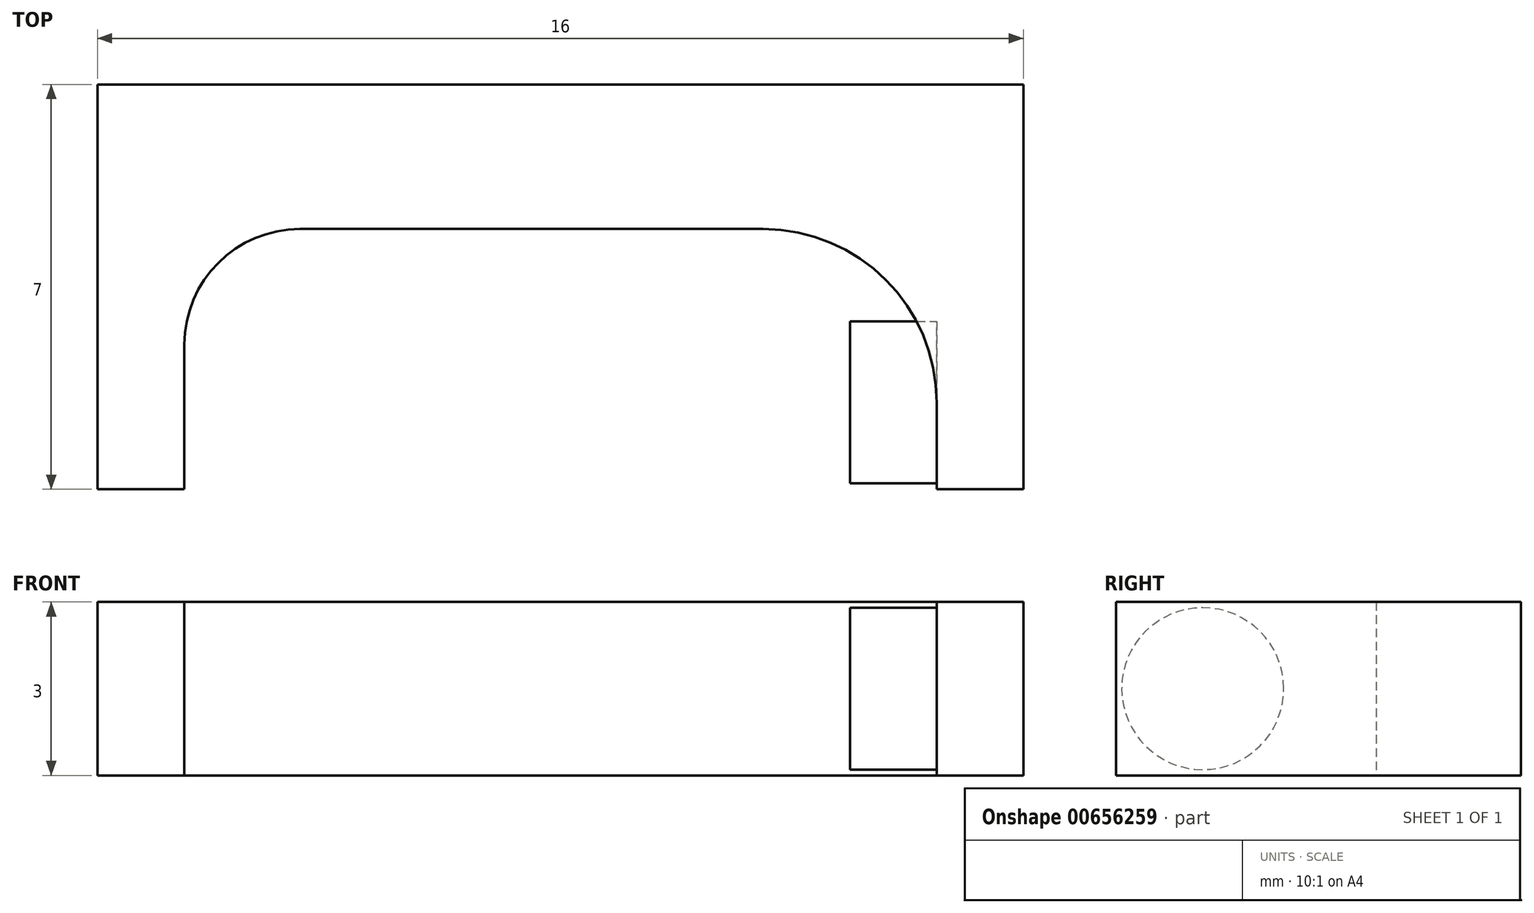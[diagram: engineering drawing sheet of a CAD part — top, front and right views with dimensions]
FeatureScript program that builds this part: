
annotation { "Feature Type Name" : "Feature", "Feature Type Description" : "" }
export const myFeature = defineFeature(function(context is Context, id is Id, definition is map)
    precondition{}
    {
        {
            var Q0;
            Q0=qCreatedBy(makeId("Top.planeOp"),FACE);
            var sketch = newSketch(context, id + "F0", { "sketchPlane" : qUnion([Q0])});
            skLineSegment(sketch, "E0", {"start": v(-1.74, -1) * mm, "end": v(-1.74, 3.5) * mm});
            skLineSegment(sketch, "E1", {"start": v(-1.74, 3.5) * mm, "end": v(11.26, 3.5) * mm});
            skLineSegment(sketch, "E2", {"start": v(11.26, 3.5) * mm, "end": v(11.26, -1) * mm});
            skLineSegment(sketch, "E3", {"start": v(-1.74, -1) * mm, "end": v(-3.24, -1) * mm});
            skLineSegment(sketch, "E4", {"start": v(-3.24, -1) * mm, "end": v(-3.24, 6) * mm});
            skLineSegment(sketch, "E5", {"start": v(-3.24, 6) * mm, "end": v(12.76, 6) * mm});
            skLineSegment(sketch, "E6", {"start": v(12.76, 6) * mm, "end": v(12.76, -1) * mm});
            skLineSegment(sketch, "E7", {"start": v(12.76, -1) * mm, "end": v(11.26, -1) * mm});
            skSolve(sketch);
        }
        {
            var Q0;
            Q0=makeQuery(id+"F0.imprint","IMPRINT",FACE,{"disambiguationData":[TD([[makeQuery(id+"F0.imprint","IMPRINT",EDGE,{"derivedFrom":sQuery(id+"F0.wireOp",EDGE,"E0")}),1.0]])]});
            extrude(context, id + "F1", {"entities" : qUnion([Q0]), "depth" : 3 * mm, "offsetDistance" : 25 * mm});
        }
        {
            var Q0;
            Q0=makeQuery(id+"F1.opExtrude","SWEPT_EDGE",EDGE,{"disambiguationData":[OSD([sQuery(id+"F0.wireOp",EDGE,"E1"),sQuery(id+"F0.wireOp",EDGE,"E2")])]});
            fillet(context, id + "F2", {"entities" : qUnion([Q0]), "radius" : 3 * mm, "tangentPropagation" : true, "allowEdgeOverflow" : false});
        }
        {
            var Q0;
            Q0=makeQuery(id+"F1.opExtrude","SWEPT_EDGE",EDGE,{"disambiguationData":[OSD([sQuery(id+"F0.wireOp",EDGE,"E0"),sQuery(id+"F0.wireOp",EDGE,"E1")])]});
            fillet(context, id + "F3", {"entities" : qUnion([Q0]), "radius" : 2 * mm, "tangentPropagation" : true, "allowEdgeOverflow" : false});
        }
        {
            var Q0;
            Q0=makeQuery(id+"F1.opExtrude","SWEPT_FACE",FACE,{"disambiguationData":[OSD([sQuery(id+"F0.wireOp",EDGE,"E2")])]});
            var sketch = newSketch(context, id + "F4", { "sketchPlane" : qUnion([Q0])});
            skLineSegment(sketch, "E8.0", {"start": v(-0.5, 0) * mm, "end": v(1, 0) * mm, "construction": true});
            skLineSegment(sketch, "E8.1", {"start": v(-0.5, 3) * mm, "end": v(1, 3) * mm, "construction": true});
            skLineSegment(sketch, "E8.2", {"start": v(1, 3) * mm, "end": v(1, 0) * mm, "construction": true});
            skLineSegment(sketch, "E9", {"start": v(1, 1.5) * mm, "end": v(-0.5, 1.5) * mm, "construction": true});
            skCircle(sketch, "E10", {"center": v(-0.5, 1.5) * mm, "radius": 1.4 * mm});
            skSolve(sketch);
        }
        {
            var Q0;
            {var subQ0=sQuery(id+"F4.wireOp",EDGE,"E10");var subQ1=sQuery(id+"F0.wireOp",EDGE,"E2");var subQ2=makeQuery(id+"F4.imprint","INTERSECT",VERTEX,{"derivedFrom":[makeQuery(id+"F1.opExtrude","CAP_EDGE",EDGE,{"disambiguationData":[OSD([subQ1])],"isStart":false}),subQ0]});Q0=makeQuery(id+"F4.imprint","IMPRINT",FACE,{"disambiguationData":[TD([[makeQuery(id+"F4.imprint","IMPRINT",EDGE,{"disambiguationData":[TD([[subQ2,-1.0]])],"derivedFrom":subQ0}),1.0]])]});}
            var Q1;
            Q1=sQuery(id+"F4.wireOp",EDGE,"E10");
            extrude(context, id + "F5", {"entities" : qUnion([Q0]), "surfaceEntities" : qUnion([Q1]), "depth" : 1.5 * mm, "offsetDistance" : 25 * mm});
        }
    });
